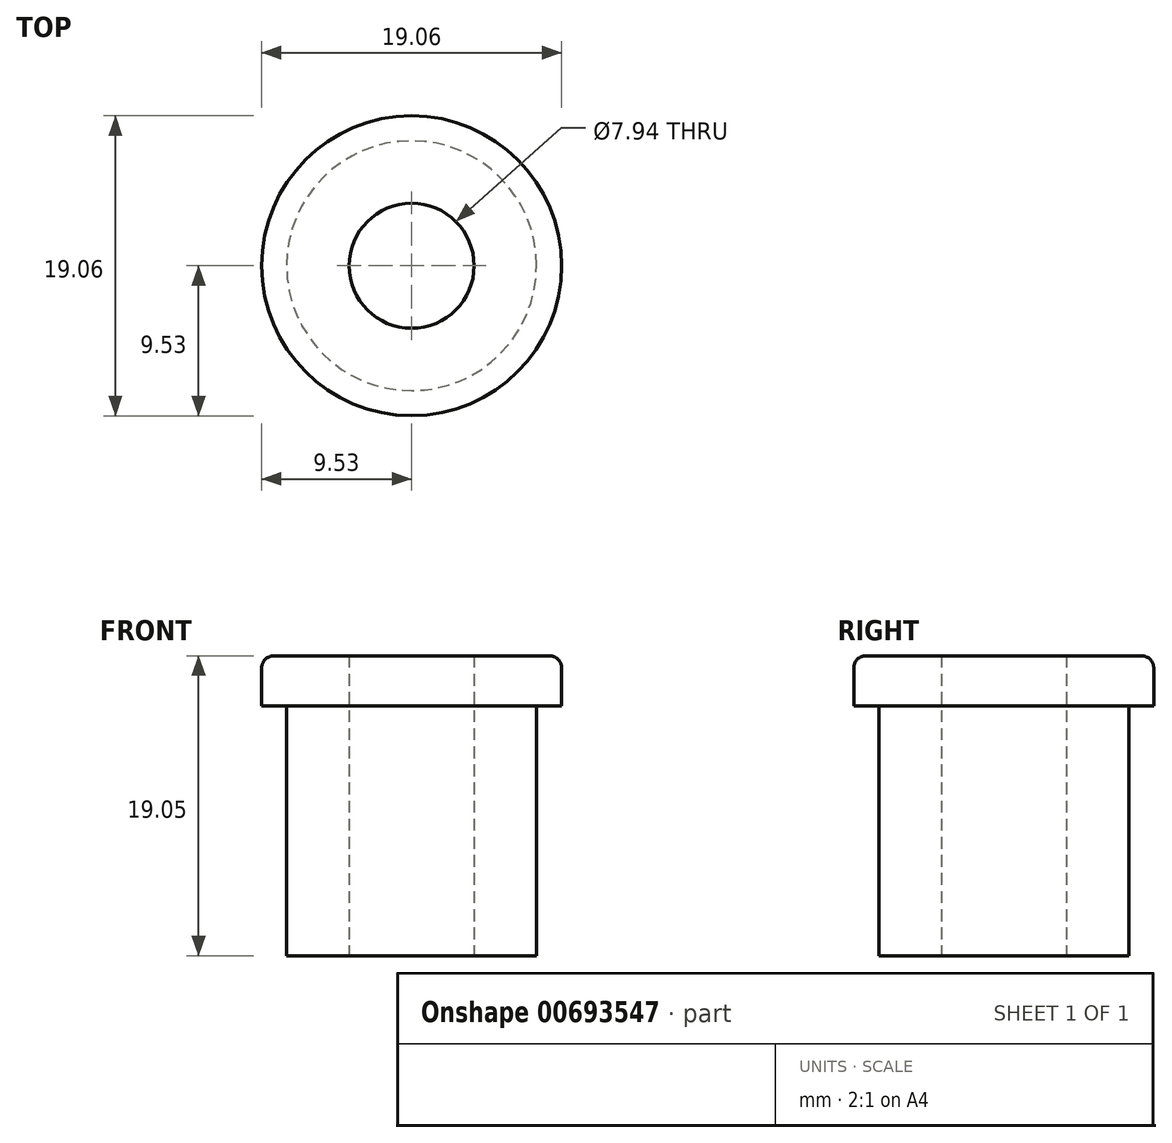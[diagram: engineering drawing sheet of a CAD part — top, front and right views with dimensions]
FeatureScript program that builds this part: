
annotation { "Feature Type Name" : "Feature", "Feature Type Description" : "" }
export const myFeature = defineFeature(function(context is Context, id is Id, definition is map)
    precondition{}
    {
        {
            var Q0;
            Q0=qCreatedBy(makeId("Front.planeOp"),FACE);
            var sketch = newSketch(context, id + "F0", { "sketchPlane" : qUnion([Q0])});
            skLineSegment(sketch, "E0", {"start": v(0, 0) * mm, "end": v(9.53, 0) * mm});
            skLineSegment(sketch, "E1", {"start": v(9.53, 0) * mm, "end": v(9.53, -3.17) * mm});
            skLineSegment(sketch, "E2", {"start": v(9.52, -3.17) * mm, "end": v(7.94, -3.17) * mm});
            skLineSegment(sketch, "E3", {"start": v(7.94, -3.17) * mm, "end": v(7.94, -19.05) * mm});
            skLineSegment(sketch, "E4", {"start": v(7.94, -19.05) * mm, "end": v(0, -19.05) * mm});
            skLineSegment(sketch, "E5", {"start": v(0, -19.05) * mm, "end": v(0, 0) * mm, "construction": true});
            skLineSegment(sketch, "E6", {"start": v(0, 0) * mm, "end": v(0, -19.05) * mm});
            skSolve(sketch);
        }
        {
            var Q0;
            Q0=makeQuery(id+"F0.imprint","IMPRINT",FACE,{"disambiguationData":[TD([[makeQuery(id+"F0.imprint","IMPRINT",EDGE,{"derivedFrom":sQuery(id+"F0.wireOp",EDGE,"E0")}),-1.0]])]});
            var Q1;
            Q1=sQuery(id+"F0.wireOp",EDGE,"E6");
            revolve(context, id + "F1", {"entities" : qUnion([Q0]), "axis" : qUnion([Q1]), "revolveType" : RevolveType.FULL});
        }
        {
            var Q0;
            Q0=makeQuery(id+"F1.opRevolve","SWEPT_EDGE",EDGE,{"disambiguationData":[OSD([sQuery(id+"F0.wireOp",EDGE,"E0"),sQuery(id+"F0.wireOp",EDGE,"E1")])]});
            fillet(context, id + "F2", {"entities" : qUnion([Q0]), "radius" : 0.76 * mm, "tangentPropagation" : true, "allowEdgeOverflow" : false});
        }
        {
            var Q0;
            Q0=makeQuery(id+"F1.opRevolve","SWEPT_FACE",FACE,{"disambiguationData":[OSD([sQuery(id+"F0.wireOp",EDGE,"E0")])]});
            var sketch = newSketch(context, id + "F3", { "sketchPlane" : qUnion([Q0])});
            skPoint(sketch, "E7", {"position": v(0, 0) * mm});
            skSolve(sketch);
        }
        {
            var Q0;
            Q0=sQuery(id+"F3.wireOp",VERTEX,"E7");
            var Q1;
            Q1=makeQuery(id+"F1.opRevolve","SWEPT_BODY",BODY,{"disambiguationData":[OSD([sQuery(id+"F0.wireOp",EDGE,"E0"),sQuery(id+"F0.wireOp",EDGE,"E1"),sQuery(id+"F0.wireOp",EDGE,"E2"),sQuery(id+"F0.wireOp",EDGE,"E3"),sQuery(id+"F0.wireOp",EDGE,"E4"),sQuery(id+"F0.wireOp",EDGE,"E6")])]});
            hole(context, id + "F4", {"style" : HoleStyle.SIMPLE, "endStyle" : HoleEndStyle.THROUGH, "standardTappedOrClearance" : lookupTablePath({ "standard" : "ANSI", "engagement" : "75%", "pitch" : "16 tpi", "size" : "3/8", "type" : "Tapped" }), "standardBlindInLast" : lookupTablePath({ "standard" : "ANSI", "engagement" : "75%", "pitch" : "16 tpi", "size" : "3/8", "type" : "Tapped" }), "holeDiameter" : 7.94 * mm, "majorDiameter" : 9.52 * mm, "showTappedDepth" : true, "isTappedThrough" : true, "tappedDepth" : 15.24 * mm, "tapClearance" : 3, "locations" : qUnion([Q0]), "scope" : qUnion([Q1]), "startStyle" : HoleStartStyle.SKETCH});
        }
    });
